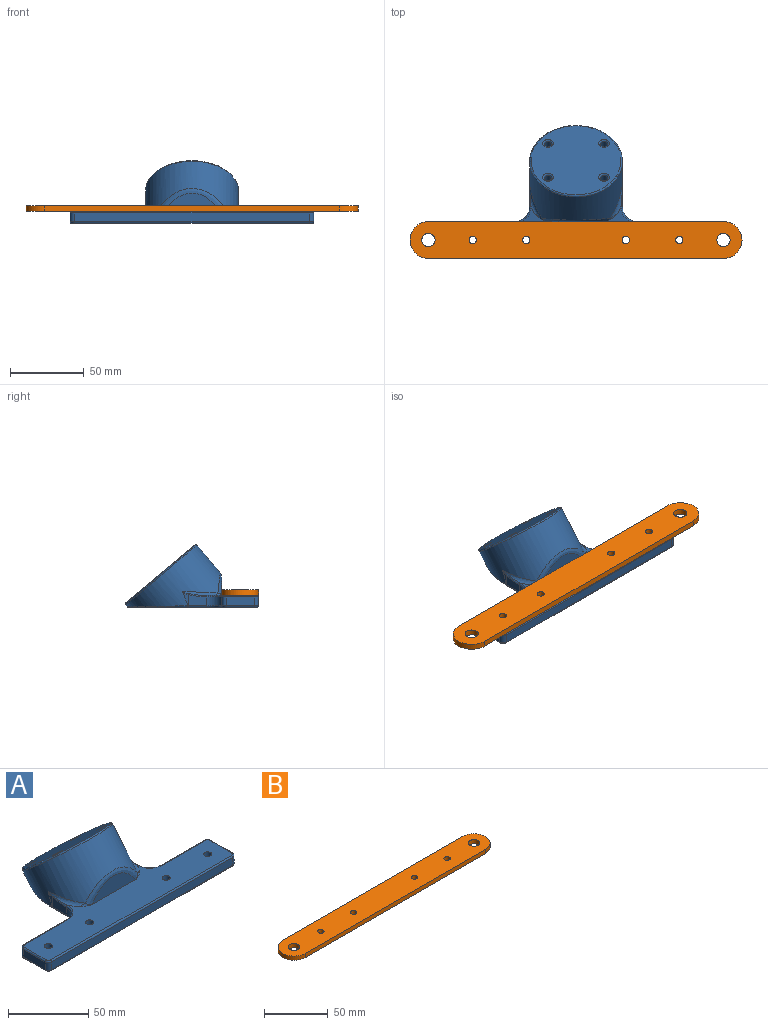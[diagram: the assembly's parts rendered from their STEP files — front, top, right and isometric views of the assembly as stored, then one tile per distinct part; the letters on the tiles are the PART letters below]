
ASSEMBLY  parts=2 mates=1
PART A: 87 faces, bbox 167.4x94.3x70.5 mm
  f0: cylinder r=31.5mm len=70.11mm, axis (0,-0.64,-0.77), area 3711.5mm2, adj f1,f2,f32,f33,f38,f54,f61,f79
  f1: cylinder r=31.5mm len=9.22mm, axis (0,0,-1), area 15.2mm2, adj f0,f12,f54,f59,f61
  f2: cylinder r=31.5mm len=9.22mm, axis (0,0,-1), area 15.2mm2, adj f0,f3,f38,f61,f63
  f3: plane 12.5x7.64mm, normal (-1,0,0), area 82.1mm2, adj f2,f30,f39,f40,f65
  f4: plane 38x6mm, normal (0,1,0), area 228mm2, adj f30,f34,f42,f69
  f5: plane 19x6mm, normal (-1,0,0), area 114mm2, adj f34,f35,f44,f68
  f6: plane 159x6mm, normal (0,-1,0), area 954mm2, adj f35,f36,f46,f64
  f7: plane 19x6mm, normal (1,0,0), area 114mm2, adj f36,f37,f48,f60
  f8: plane 38x6mm, normal (0,1,0), area 228mm2, adj f31,f37,f50,f56
  f9: cylinder r=2.5mm len=7mm, axis (0,0,-1), area 110mm2, adj f14,f80
  f10: cylinder r=2.5mm len=7mm, axis (0,0,-1), area 110mm2, adj f14,f81
  f11: cylinder r=2.5mm len=7mm, axis (0,0,-1), area 110mm2, adj f14,f82
  f12: plane 12.5x7.64mm, normal (1,0,0), area 82.1mm2, adj f1,f31,f52,f53,f57
  f13: cylinder r=2.5mm len=7mm, axis (0,0,-1), area 110mm2, adj f14,f83
  f14: plane 164.95x36.63mm, normal (0,0,1), area 3853.3mm2, adj f9,f10,f11,f13,f29,f32,f33,f40
  f15: plane 163x87.15mm, normal (0,0,-1), area 6445.2mm2, adj f55,f56,f57,f58,f59,f60,f61,f62
  f16: plane 61x46.73mm, normal (0,0.64,0.77), area 2759.6mm2, adj f75,f76,f77,f78,f79
  f17: cylinder r=5mm len=35.37mm, axis (0,-0.64,-0.77), area 1028.8mm2, adj f19,f74
  f18: cylinder r=2.6mm len=8.71mm, axis (0,-0.64,-0.77), area 114.4mm2, adj f19,f78
  f19: plane 10x7.66mm, normal (0,-0.64,-0.77), area 57.3mm2, adj f17,f18
  f20: cylinder r=5mm len=16.09mm, axis (0,-0.64,-0.77), area 238mm2, adj f22,f73
  f21: cylinder r=2.6mm len=8.71mm, axis (0,-0.64,-0.77), area 114.4mm2, adj f22,f77
  f22: plane 10x7.66mm, normal (0,-0.64,-0.77), area 57.3mm2, adj f20,f21
  f23: cylinder r=5mm len=35.37mm, axis (0,-0.64,-0.77), area 1028.8mm2, adj f25,f72
  f24: cylinder r=2.6mm len=8.71mm, axis (0,-0.64,-0.77), area 114.4mm2, adj f25,f76
  f25: plane 10x7.66mm, normal (0,-0.64,-0.77), area 57.3mm2, adj f23,f24
  f26: cylinder r=5mm len=16.09mm, axis (0,-0.64,-0.77), area 238mm2, adj f28,f71
  f27: cylinder r=2.6mm len=8.71mm, axis (0,-0.64,-0.77), area 114.4mm2, adj f28,f75
  f28: plane 10x7.66mm, normal (0,-0.64,-0.77), area 57.3mm2, adj f26,f27
  f29: plane 37.85x12.37mm, normal (0,-1,0), area 322.9mm2, adj f14,f85
  f30: cylinder r=10mm len=10mm, axis (0,0,1), area 94.2mm2, adj f3,f4,f41,f67
  f31: cylinder r=10mm len=10mm, axis (0,0,1), area 94.2mm2, adj f8,f12,f51,f55
  f32: bspline ~25.5x11.33mm, area 64.1mm2, adj f0,f14,f38,f39,f84
  f33: bspline ~25.5x11.33mm, area 64.1mm2, adj f0,f14,f53,f54,f86
  f34: cylinder r=3mm len=6mm, axis (0,0,-1), area 28.3mm2, adj f4,f5,f43,f70
  f35: cylinder r=3mm len=6mm, axis (0,0,-1), area 28.3mm2, adj f5,f6,f45,f66
  f36: cylinder r=3mm len=6mm, axis (0,0,1), area 28.3mm2, adj f6,f7,f47,f62
  f37: cylinder r=3mm len=6mm, axis (0,0,-1), area 28.3mm2, adj f7,f8,f49,f58
  f38: bspline ~5.43x2.47mm, area 2mm2, adj f0,f2,f32,f39
  f39: bspline ~17.62x2.98mm, area 13mm2, adj f3,f32,f38,f40
  f40: cylinder r=1mm len=1mm, axis (0,1,0), area 1.1mm2, adj f3,f14,f39,f41
  f41: torus R=11mm, axis (0,0,1), area 25.6mm2, adj f14,f30,f40,f42
  f42: cylinder r=1mm len=38mm, axis (1,0,0), area 59.7mm2, adj f4,f14,f41,f43
  f43: torus R=2mm, axis (0,0,1), area 6.5mm2, adj f14,f34,f42,f44
  f44: cylinder r=1mm len=19mm, axis (0,1,0), area 29.8mm2, adj f5,f14,f43,f45
  f45: torus R=2mm, axis (0,0,1), area 6.5mm2, adj f14,f35,f44,f46
  f46: cylinder r=1mm len=159mm, axis (-1,0,0), area 249.8mm2, adj f6,f14,f45,f47
  f47: torus R=2mm, axis (0,0,1), area 6.5mm2, adj f14,f36,f46,f48
  f48: cylinder r=1mm len=19mm, axis (0,-1,0), area 29.8mm2, adj f7,f14,f47,f49
  f49: torus R=2mm, axis (0,0,1), area 6.5mm2, adj f14,f37,f48,f50
  f50: cylinder r=1mm len=38mm, axis (1,0,0), area 59.7mm2, adj f8,f14,f49,f51
  f51: torus R=11mm, axis (0,0,1), area 25.6mm2, adj f14,f31,f50,f52
  f52: cylinder r=1mm len=1mm, axis (0,-1,0), area 1.1mm2, adj f12,f14,f51,f53
  f53: bspline ~17.62x2.98mm, area 13mm2, adj f12,f33,f52,f54
  f54: bspline ~5.43x2.47mm, area 2mm2, adj f0,f1,f33,f53
  f55: torus R=11mm, axis (0,0,1), area 25.6mm2, adj f15,f31,f56,f57
  f56: cylinder r=1mm len=38mm, axis (-1,0,0), area 59.7mm2, adj f8,f15,f55,f58
  f57: cylinder r=1mm len=12.5mm, axis (0,1,0), area 19.6mm2, adj f12,f15,f55,f59
  f58: torus R=2mm, axis (0,0,1), area 6.5mm2, adj f15,f37,f56,f60
  f59: torus R=30.5mm, axis (0,0,1), area 0.6mm2, adj f1,f15,f57,f61
  f60: cylinder r=1mm len=19mm, axis (0,1,0), area 29.8mm2, adj f7,f15,f58,f62
  f61: bspline ~63.05x47.65mm, area 131.8mm2, adj f0,f1,f2,f15,f59,f63
  f62: torus R=2mm, axis (0,0,1), area 6.5mm2, adj f15,f36,f60,f64
  f63: torus R=30.5mm, axis (0,0,1), area 0.6mm2, adj f2,f15,f61,f65
  f64: cylinder r=1mm len=159mm, axis (1,0,0), area 249.8mm2, adj f6,f15,f62,f66
  f65: cylinder r=1mm len=12.5mm, axis (0,-1,0), area 19.6mm2, adj f3,f15,f63,f67
  f66: torus R=2mm, axis (0,0,1), area 6.5mm2, adj f15,f35,f64,f68
  f67: torus R=11mm, axis (0,0,1), area 25.6mm2, adj f15,f30,f65,f69
  f68: cylinder r=1mm len=19mm, axis (0,-1,0), area 29.8mm2, adj f5,f15,f66,f70
  f69: cylinder r=1mm len=38mm, axis (-1,0,0), area 59.7mm2, adj f4,f15,f67,f70
  f70: torus R=2mm, axis (0,0,1), area 6.5mm2, adj f15,f34,f68,f69
  f71: bspline ~15.67x12mm, area 62.2mm2, adj f15,f26
  f72: bspline ~15.65x11.99mm, area 62.2mm2, adj f15,f23
  f73: bspline ~15.67x12mm, area 62.2mm2, adj f15,f20
  f74: bspline ~15.65x11.99mm, area 62.2mm2, adj f15,f17
  f75: torus R=3.6mm, axis (0,0.64,0.77), area 29.2mm2, adj f16,f27
  f76: torus R=3.6mm, axis (0,0.64,0.77), area 29.2mm2, adj f16,f24
  f77: torus R=3.6mm, axis (0,0.64,0.77), area 29.2mm2, adj f16,f21
  f78: torus R=3.6mm, axis (0,0.64,0.77), area 29.2mm2, adj f16,f18
  f79: torus R=30.5mm, axis (0,0.64,0.77), area 307.3mm2, adj f0,f16
  f80: torus R=3.5mm, axis (0,0,1), area 28.3mm2, adj f9,f15
  f81: torus R=3.5mm, axis (0,0,1), area 28.3mm2, adj f10,f15
  f82: torus R=3.5mm, axis (0,0,1), area 28.3mm2, adj f11,f15
  f83: torus R=3.5mm, axis (0,0,1), area 28.3mm2, adj f13,f15
  f84: bspline ~9.01x6.75mm, area 14.2mm2, adj f14,f32,f85
  f85: bspline ~45.78x16.11mm, area 214mm2, adj f0,f14,f29,f84,f86
  f86: bspline ~9.41x6.94mm, area 14.2mm2, adj f14,f33,f85
PART B: 12 faces, bbox 225x25x4 mm
  f0: cylinder r=12.5mm len=25mm, axis (0,0,-1), area 157.1mm2, adj f1,f8,f10,f11
  f1: plane 200x4mm, normal (0,-1,0), area 800mm2, adj f0,f2,f10,f11
  f2: cylinder r=12.5mm len=25mm, axis (0,0,-1), area 157.1mm2, adj f1,f8,f10,f11
  f3: cylinder r=2.5mm len=5mm, axis (0,0,-1), area 62.8mm2, adj f10,f11
  f4: cylinder r=2.5mm len=5mm, axis (0,0,-1), area 62.8mm2, adj f10,f11
  f5: cylinder r=2.5mm len=5mm, axis (0,0,-1), area 62.8mm2, adj f10,f11
  f6: cylinder r=4.5mm len=9mm, axis (0,0,-1), area 113.1mm2, adj f10,f11
  f7: cylinder r=4.5mm len=9mm, axis (0,0,-1), area 113.1mm2, adj f10,f11
  f8: plane 200x4mm, normal (0,1,0), area 800mm2, adj f0,f2,f10,f11
  f9: cylinder r=2.5mm len=5mm, axis (0,0,-1), area 62.8mm2, adj f10,f11
  f10: plane 225x25mm, normal (0,0,1), area 5285.1mm2, adj f0,f1,f2,f3,f4,f5,f6,f7
  f11: plane 225x25mm, normal (0,0,-1), area 5285.1mm2, adj f0,f1,f2,f3,f4,f5,f6,f7
PLACE A t=(-33.75,35,0)mm
PLACE B t=(-33.75,112.5,8)mm
MATE fastened A.f9 <-> B.f3  axis (0,0,1) through (-103.75,0,8)mm
